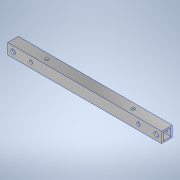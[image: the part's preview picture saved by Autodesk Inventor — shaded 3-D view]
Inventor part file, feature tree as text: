
AUTODESK INVENTOR PART (.ipt)
format: ipt  version: 2020.3 (Build 243373000, 373)  size: 167,424 bytes
history: native  units: mm
features: sketch x6, extrude x3, hole x3, other x1
ambient origin geometry x8: Origin, YZ Plane, XZ Plane, XY Plane, X Axis, Y Axis, Z Axis, Center Point
bodies: Body1 (feature_tree)
feature tree (13):
  other  "ソリッド1"
  extrude  "押し出し1"  Depth=9.0mm
  hole  "穴1"  [1 undecoded]
  hole  "穴2"  [1 undecoded]
  extrude  "押し出し2"  Depth=6.6mm
  extrude  "押し出し3"  Depth=1.2mm
  hole  "穴3"  [1 undecoded]
  sketch  "スケッチ1"
  sketch  "スケッチ2"
  sketch  "スケッチ3"
  sketch  "スケッチ4"
  sketch  "スケッチ5"
  sketch  "スケッチ6"
note: 3 required parameter values undecoded (feature->parameter linkage not recoverable at this tier; creation-order binding heuristic only, values carry confidence <= 0.55)
